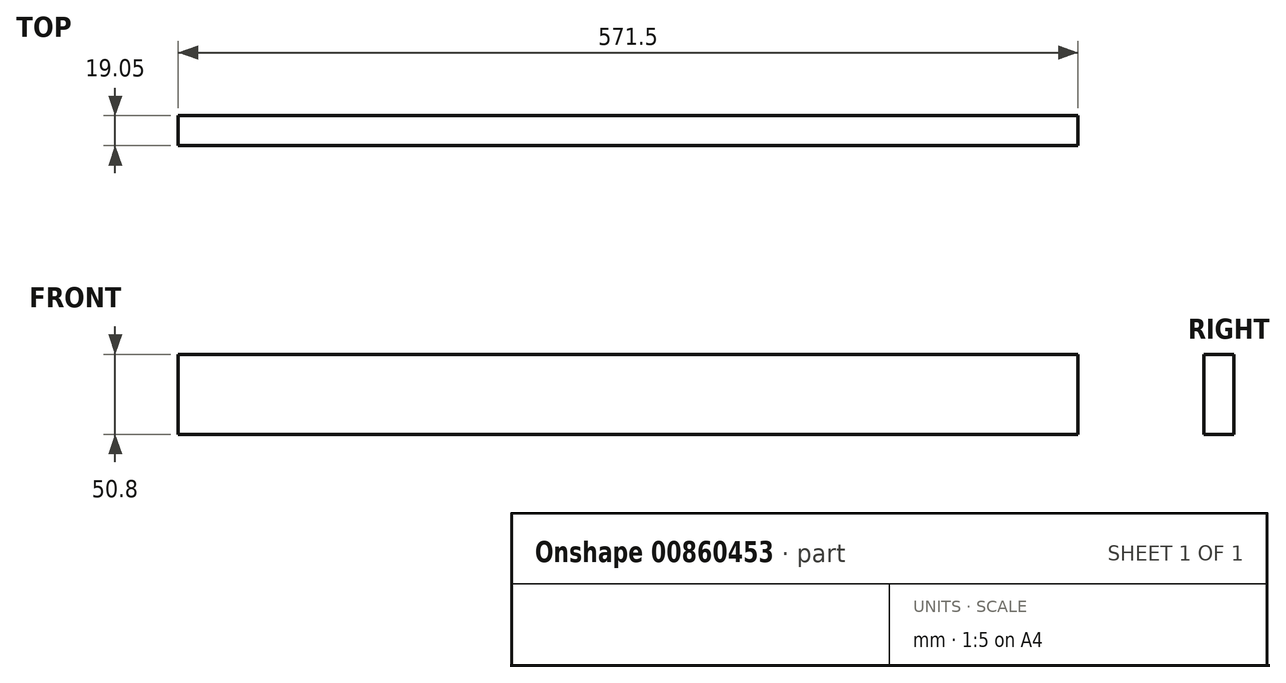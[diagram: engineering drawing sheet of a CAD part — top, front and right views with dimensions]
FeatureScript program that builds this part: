
annotation { "Feature Type Name" : "Feature", "Feature Type Description" : "" }
export const myFeature = defineFeature(function(context is Context, id is Id, definition is map)
    precondition{}
    {
        {
            var Q0;
            Q0=qCreatedBy(makeId("Front.planeOp"),FACE);
            var sketch = newSketch(context, id + "F0", { "sketchPlane" : qUnion([Q0])});
            skLineSegment(sketch, "E0.bottom", {"start": v(285.75, 25.4) * mm, "end": v(-285.75, 25.4) * mm});
            skLineSegment(sketch, "E0.top", {"start": v(285.75, -25.4) * mm, "end": v(-285.75, -25.4) * mm});
            skLineSegment(sketch, "E0.left", {"start": v(285.75, 25.4) * mm, "end": v(285.75, -25.4) * mm});
            skLineSegment(sketch, "E0.right", {"start": v(-285.75, 25.4) * mm, "end": v(-285.75, -25.4) * mm});
            skPoint(sketch, "E0.middle", {"position": v(0, 0) * mm});
            skSolve(sketch);
        }
        {
            var Q0;
            Q0=makeQuery(id+"F0.imprint","IMPRINT",FACE,{"disambiguationData":[TD([[makeQuery(id+"F0.imprint","IMPRINT",EDGE,{"derivedFrom":sQuery(id+"F0.wireOp",EDGE,"E0.bottom")}),1.0]])]});
            extrude(context, id + "F1", {"entities" : qUnion([Q0]), "depth" : 19.05 * mm, "offsetDistance" : 25.4 * mm});
        }
    });
